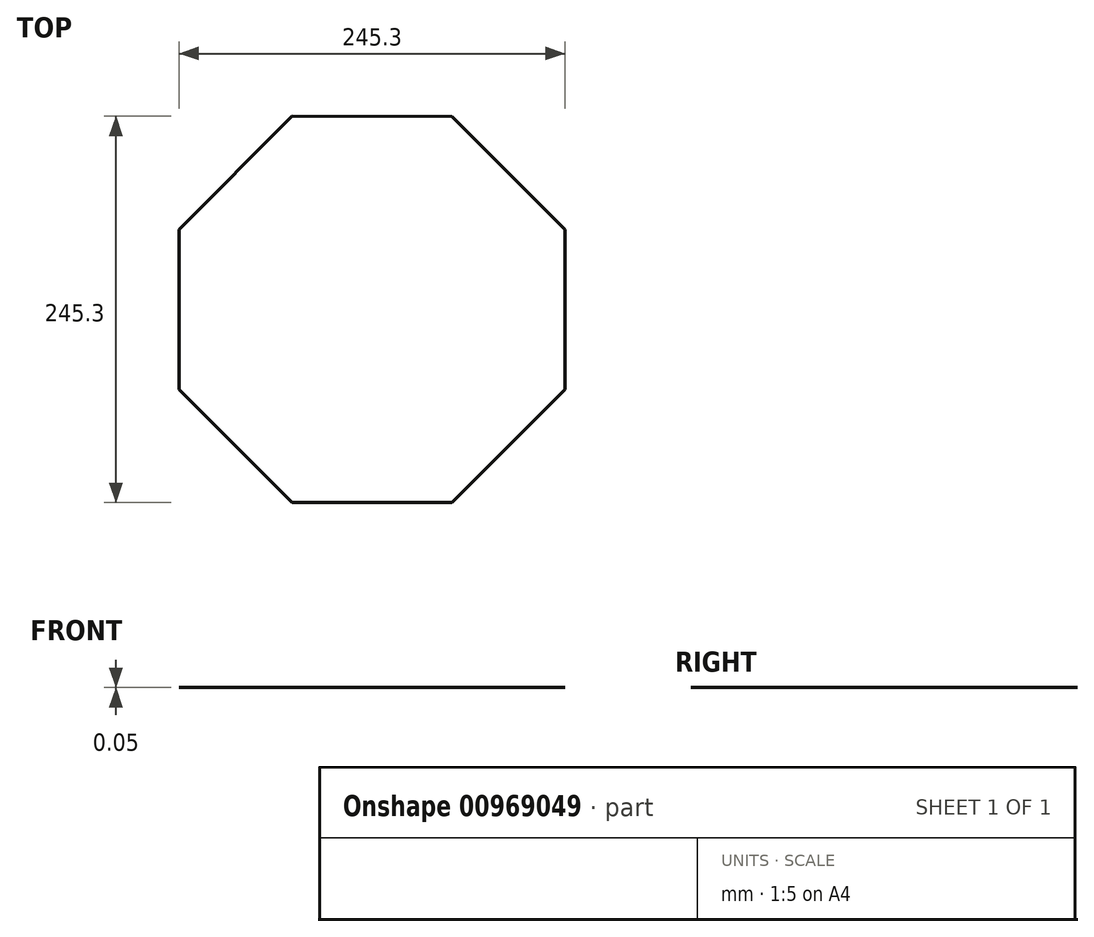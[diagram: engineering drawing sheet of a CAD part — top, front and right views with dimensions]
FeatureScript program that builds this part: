
annotation { "Feature Type Name" : "Feature", "Feature Type Description" : "" }
export const myFeature = defineFeature(function(context is Context, id is Id, definition is map)
    precondition{}
    {
        {
            var Q0;
            Q0=qCreatedBy(makeId("Top.planeOp"),FACE);
            var sketch = newSketch(context, id + "F0", { "sketchPlane" : qUnion([Q0])});
            skLineSegment(sketch, "E0.0", {"start": v(122.63, -50.82) * mm, "end": v(50.78, -122.65) * mm});
            skLineSegment(sketch, "E0.1", {"start": v(50.78, -122.65) * mm, "end": v(-50.82, -122.63) * mm});
            skLineSegment(sketch, "E0.2", {"start": v(-50.82, -122.63) * mm, "end": v(-122.65, -50.78) * mm});
            skLineSegment(sketch, "E0.3", {"start": v(-122.65, -50.78) * mm, "end": v(-122.63, 50.82) * mm});
            skLineSegment(sketch, "E0.4", {"start": v(-122.63, 50.82) * mm, "end": v(-50.78, 122.65) * mm});
            skLineSegment(sketch, "E0.5", {"start": v(-50.78, 122.65) * mm, "end": v(50.82, 122.63) * mm});
            skLineSegment(sketch, "E0.6", {"start": v(50.82, 122.63) * mm, "end": v(122.65, 50.78) * mm});
            skLineSegment(sketch, "E0.7", {"start": v(122.65, 50.78) * mm, "end": v(122.63, -50.82) * mm});
            skPoint(sketch, "E0.0.midPoint", {"position": v(86.7, -86.74) * mm});
            skLineSegment(sketch, "E1", {"start": v(-50.78, 122.65) * mm, "end": v(-50.82, -122.63) * mm, "construction": true});
            skLineSegment(sketch, "E2", {"start": v(-122.63, 50.82) * mm, "end": v(122.65, 50.78) * mm, "construction": true});
            skSolve(sketch);
        }
        {
            var Q0;
            Q0=makeQuery(id+"F0.imprint","IMPRINT",FACE,{"disambiguationData":[TD([[makeQuery(id+"F0.imprint","IMPRINT",EDGE,{"derivedFrom":sQuery(id+"F0.wireOp",EDGE,"E0.0")}),-1.0]])]});
            extrude(context, id + "F1", {"entities" : qUnion([Q0]), "depth" : 0.05 * mm, "offsetDistance" : 25.4 * mm});
        }
    });
